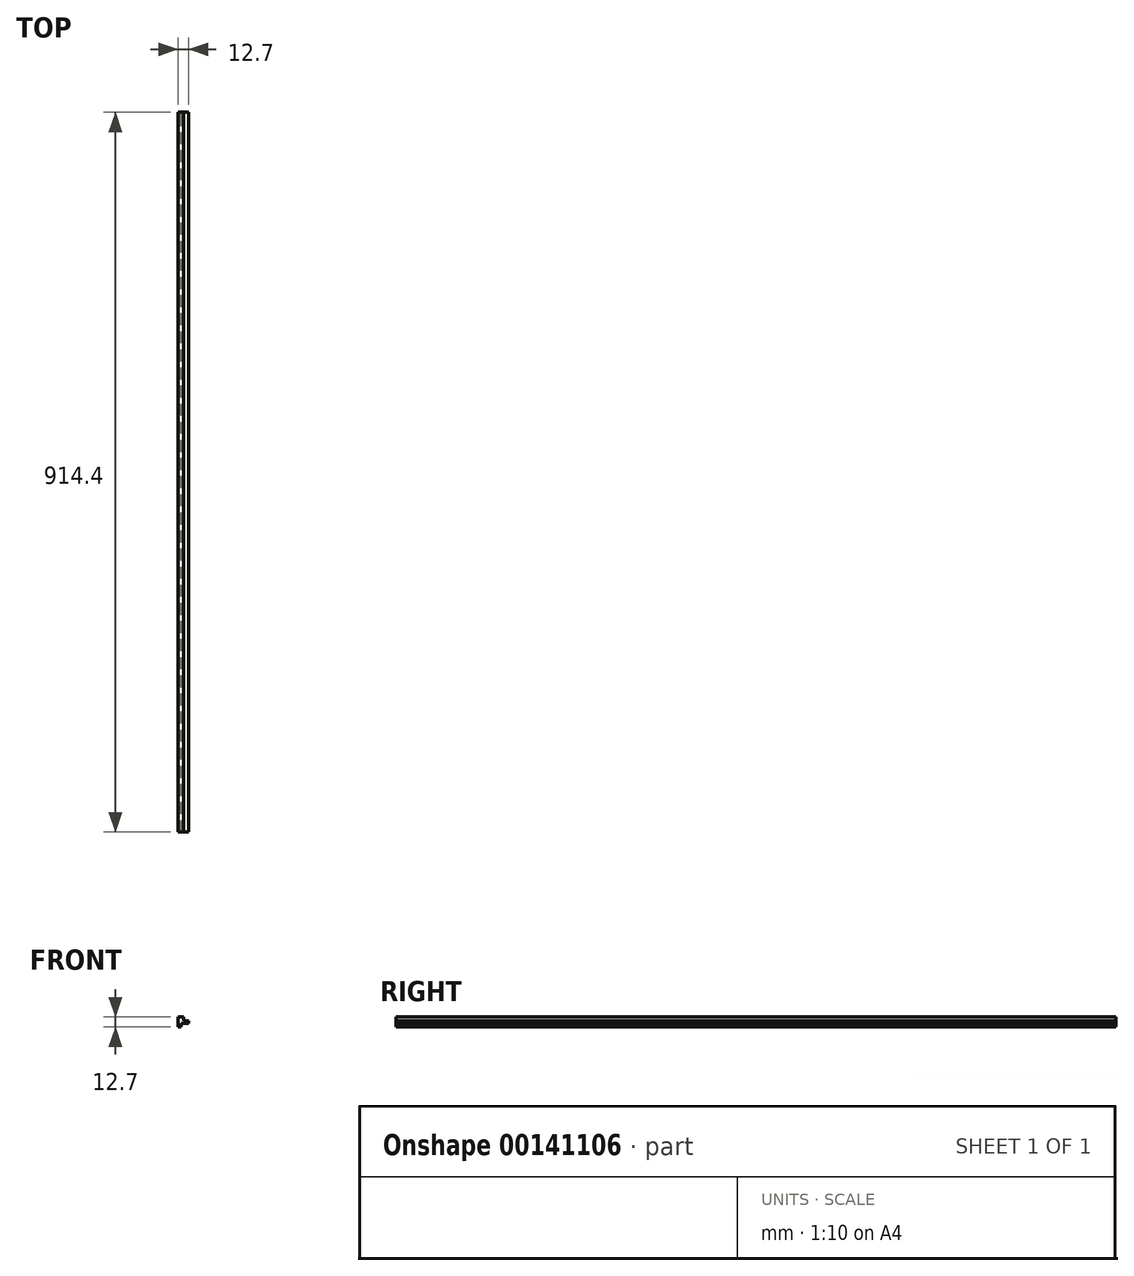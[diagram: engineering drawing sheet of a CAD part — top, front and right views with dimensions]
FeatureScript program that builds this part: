
annotation { "Feature Type Name" : "Feature", "Feature Type Description" : "" }
export const myFeature = defineFeature(function(context is Context, id is Id, definition is map)
    precondition{}
    {
        {
            var Q0;
            Q0=qCreatedBy(makeId("Front.planeOp"),FACE);
            var sketch = newSketch(context, id + "F0", { "sketchPlane" : qUnion([Q0])});
            skLineSegment(sketch, "E0.bottom", {"start": v(0, 0) * mm, "end": v(12.7, 0) * mm});
            skLineSegment(sketch, "E0.top", {"start": v(0, 12.7) * mm, "end": v(12.7, 12.7) * mm});
            skLineSegment(sketch, "E0.left", {"start": v(0, 0) * mm, "end": v(0, 12.7) * mm});
            skLineSegment(sketch, "E0.right", {"start": v(12.7, 0) * mm, "end": v(12.7, 12.7) * mm});
            skSolve(sketch);
        }
        {
            var Q0;
            Q0 = qSketchRegion(id + "F0", true);
            extrude(context, id + "F1", {"entities" : qUnion([Q0]), "depth" : 914.4 * mm});
        }
        {
            var Q0;
            Q0=qCreatedBy(makeId("Front.planeOp"),FACE);
            var sketch = newSketch(context, id + "F2", { "sketchPlane" : qUnion([Q0])});
            skLineSegment(sketch, "E1.bottom", {"start": v(3.17, 4.76) * mm, "end": v(12.7, 4.76) * mm});
            skLineSegment(sketch, "E1.top", {"start": v(3.18, 0) * mm, "end": v(12.7, 0) * mm});
            skLineSegment(sketch, "E1.left", {"start": v(3.18, 4.76) * mm, "end": v(3.18, 0) * mm});
            skLineSegment(sketch, "E1.right", {"start": v(12.7, 4.76) * mm, "end": v(12.7, 0) * mm});
            skSolve(sketch);
        }
        {
            var Q0;
            Q0 = qSketchRegion(id + "F2", true);
            extrude(context, id + "F3", {"entities" : qUnion([Q0]), "operationType" : NewBodyOperationType.REMOVE, "endBound" : BoundingType.THROUGH_ALL, "depth" : 25.4 * mm});
        }
        {
            var Q0;
            Q0=qCreatedBy(makeId("Front.planeOp"),FACE);
            var sketch = newSketch(context, id + "F4", { "sketchPlane" : qUnion([Q0])});
            skLineSegment(sketch, "E2.bottom", {"start": v(12.7, 12.7) * mm, "end": v(6.35, 12.7) * mm});
            skLineSegment(sketch, "E2.top", {"start": v(12.7, 7.94) * mm, "end": v(6.35, 7.94) * mm});
            skLineSegment(sketch, "E2.left", {"start": v(12.7, 12.7) * mm, "end": v(12.7, 7.94) * mm});
            skLineSegment(sketch, "E2.right", {"start": v(6.35, 12.7) * mm, "end": v(6.35, 7.94) * mm});
            skSolve(sketch);
        }
        {
            var Q0;
            Q0 = qSketchRegion(id + "F4", true);
            extrude(context, id + "F5", {"entities" : qUnion([Q0]), "operationType" : NewBodyOperationType.REMOVE, "endBound" : BoundingType.THROUGH_ALL, "depth" : 25.4 * mm});
        }
    });
